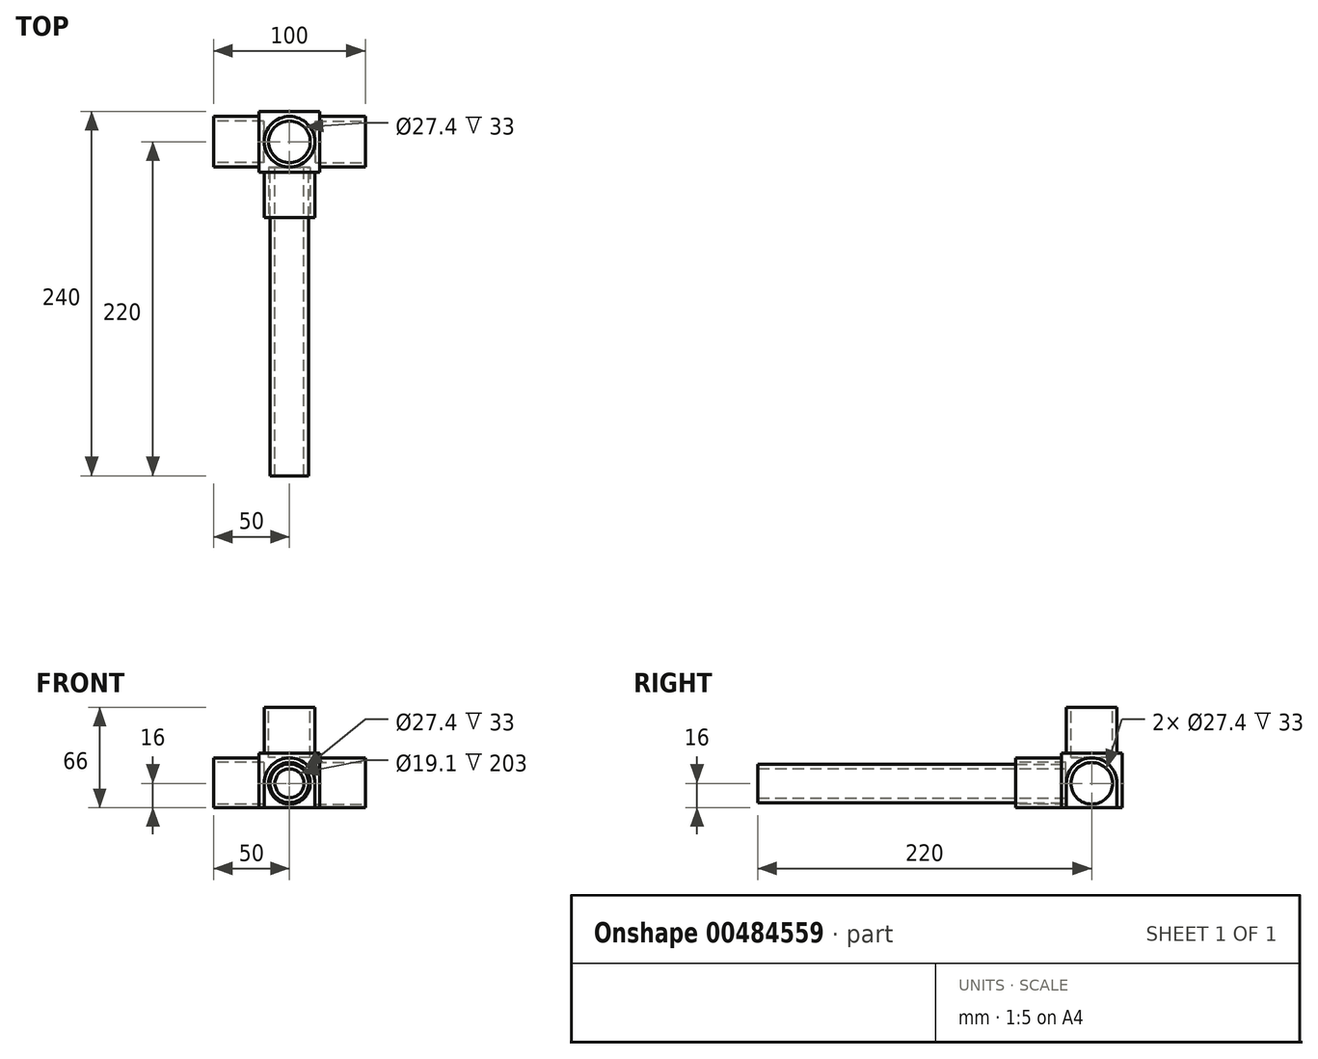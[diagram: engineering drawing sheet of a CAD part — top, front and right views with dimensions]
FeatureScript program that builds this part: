
annotation { "Feature Type Name" : "Feature", "Feature Type Description" : "" }
export const myFeature = defineFeature(function(context is Context, id is Id, definition is map)
    precondition{}
    {
        {
            var Q0;
            Q0=qCreatedBy(makeId("Front.planeOp"),FACE);
            var sketch = newSketch(context, id + "F0", { "sketchPlane" : qUnion([Q0])});
            skLineSegment(sketch, "E0.bottom", {"start": v(20, 20) * mm, "end": v(-20, 20) * mm});
            skLineSegment(sketch, "E0.top", {"start": v(20, -20) * mm, "end": v(-20, -20) * mm});
            skLineSegment(sketch, "E0.left", {"start": v(20, 20) * mm, "end": v(20, -20) * mm});
            skLineSegment(sketch, "E0.right", {"start": v(-20, 20) * mm, "end": v(-20, -20) * mm});
            skPoint(sketch, "E0.middle", {"position": v(0, 0) * mm});
            skSolve(sketch);
        }
        {
            var Q0;
            Q0=makeQuery(id+"F0.imprint","IMPRINT",FACE,{"disambiguationData":[TD([[makeQuery(id+"F0.imprint","IMPRINT",EDGE,{"derivedFrom":sQuery(id+"F0.wireOp",EDGE,"E0.bottom")}),1.0]])]});
            extrude(context, id + "F1", {"entities" : qUnion([Q0]), "endBound" : BoundingType.SYMMETRIC, "depth" : 40 * mm});
        }
        {
            var Q0;
            Q0=makeQuery(id+"F1.opExtrude","CAP_FACE",FACE,{"disambiguationData":[OSD([sQuery(id+"F0.wireOp",EDGE,"E0.bottom"),sQuery(id+"F0.wireOp",EDGE,"E0.top"),sQuery(id+"F0.wireOp",EDGE,"E0.left"),sQuery(id+"F0.wireOp",EDGE,"E0.right")])],"isStart":false});
            var sketch = newSketch(context, id + "F2", { "sketchPlane" : qUnion([Q0])});
            skLineSegment(sketch, "E1.bottom", {"start": v(20, 20) * mm, "end": v(-20, 20) * mm});
            skLineSegment(sketch, "E1.top", {"start": v(20, -20) * mm, "end": v(-20, -20) * mm});
            skLineSegment(sketch, "E1.left", {"start": v(20, 20) * mm, "end": v(20, -20) * mm});
            skLineSegment(sketch, "E1.right", {"start": v(-20, 20) * mm, "end": v(-20, -20) * mm});
            skPoint(sketch, "E1.middle", {"position": v(0, 0) * mm});
            skCircle(sketch, "E2", {"center": v(0, 0) * mm, "radius": 12.7 * mm});
            skCircle(sketch, "E3.0", {"center": v(0, 0) * mm, "radius": 9.55 * mm});
            skCircle(sketch, "E4.0", {"center": v(0, 0) * mm, "radius": 13.7 * mm});
            skCircle(sketch, "E5.0", {"center": v(0, 0) * mm, "radius": 16.7 * mm});
            skSolve(sketch);
        }
        {
            var Q0;
            Q0=makeQuery(id+"F2.imprint","IMPRINT",FACE,{"disambiguationData":[TD([[makeQuery(id+"F2.imprint","IMPRINT",EDGE,{"derivedFrom":sQuery(id+"F2.wireOp",EDGE,"E2")}),-1.0]])]});
            var Q1;
            Q1=makeQuery(id+"F2.imprint","IMPRINT",FACE,{"disambiguationData":[TD([[makeQuery(id+"F2.imprint","IMPRINT",EDGE,{"derivedFrom":sQuery(id+"F2.wireOp",EDGE,"E2")}),1.0]])]});
            var Q2;
            Q2=makeQuery(id+"F2.imprint","IMPRINT",FACE,{"disambiguationData":[TD([[makeQuery(id+"F2.imprint","IMPRINT",EDGE,{"derivedFrom":sQuery(id+"F2.wireOp",EDGE,"E3.0")}),1.0]])]});
            extrude(context, id + "F3", {"entities" : qUnion([Q0, Q1, Q2]), "operationType" : NewBodyOperationType.REMOVE, "oppositeDirection" : true, "depth" : 3 * mm});
        }
        {
            var Q0;
            Q0=makeQuery(id+"F2.imprint","IMPRINT",FACE,{"disambiguationData":[TD([[makeQuery(id+"F2.imprint","IMPRINT",EDGE,{"derivedFrom":sQuery(id+"F2.wireOp",EDGE,"E2")}),1.0]])]});
            extrude(context, id + "F4", {"entities" : qUnion([Q0]), "depth" : 200 * mm});
        }
        {
            var Q0;
            Q0=makeQuery(id+"F4.opExtrude","CAP_FACE",FACE,{"disambiguationData":[OSD([sQuery(id+"F2.wireOp",EDGE,"E2"),sQuery(id+"F2.wireOp",EDGE,"E3.0")])],"isStart":true});
            extrude(context, id + "F5", {"entities" : qUnion([Q0]), "operationType" : NewBodyOperationType.ADD, "depth" : 3 * mm});
        }
        {
            var Q0;
            Q0=makeQuery(id+"F2.imprint","IMPRINT",FACE,{"disambiguationData":[TD([[makeQuery(id+"F2.imprint","IMPRINT",EDGE,{"derivedFrom":sQuery(id+"F2.wireOp",EDGE,"E4.0")}),-1.0]])]});
            extrude(context, id + "F6", {"entities" : qUnion([Q0]), "operationType" : NewBodyOperationType.ADD, "depth" : 30 * mm});
        }
        {
            var Q0;
            Q0=makeQuery(id+"F1.opExtrude","SWEPT_FACE",FACE,{"disambiguationData":[OSD([sQuery(id+"F0.wireOp",EDGE,"E0.left")])]});
            var sketch = newSketch(context, id + "F7", { "sketchPlane" : qUnion([Q0])});
            skLineSegment(sketch, "E6.bottom", {"start": v(20, 20) * mm, "end": v(-20, 20) * mm});
            skLineSegment(sketch, "E6.top", {"start": v(20, -20) * mm, "end": v(-20, -20) * mm});
            skLineSegment(sketch, "E6.left", {"start": v(20, 20) * mm, "end": v(20, -20) * mm});
            skLineSegment(sketch, "E6.right", {"start": v(-20, 20) * mm, "end": v(-20, -20) * mm});
            skPoint(sketch, "E6.middle", {"position": v(0, 0) * mm});
            skCircle(sketch, "E7", {"center": v(0, 0) * mm, "radius": 12.7 * mm});
            skCircle(sketch, "E8.0", {"center": v(0, 0) * mm, "radius": 9.55 * mm});
            skCircle(sketch, "E9.0", {"center": v(0, 0) * mm, "radius": 13.7 * mm});
            skCircle(sketch, "E10.0", {"center": v(0, 0) * mm, "radius": 16.7 * mm});
            skSolve(sketch);
        }
        {
            var Q0;
            Q0=makeQuery(id+"F7.imprint","IMPRINT",FACE,{"disambiguationData":[TD([[makeQuery(id+"F7.imprint","IMPRINT",EDGE,{"derivedFrom":sQuery(id+"F7.wireOp",EDGE,"E7")}),-1.0]])]});
            var Q1;
            Q1=makeQuery(id+"F7.imprint","IMPRINT",FACE,{"disambiguationData":[TD([[makeQuery(id+"F7.imprint","IMPRINT",EDGE,{"derivedFrom":sQuery(id+"F7.wireOp",EDGE,"E7")}),1.0]])]});
            var Q2;
            Q2=makeQuery(id+"F7.imprint","IMPRINT",FACE,{"disambiguationData":[TD([[makeQuery(id+"F7.imprint","IMPRINT",EDGE,{"derivedFrom":sQuery(id+"F7.wireOp",EDGE,"E8.0")}),1.0]])]});
            extrude(context, id + "F8", {"entities" : qUnion([Q0, Q1, Q2]), "operationType" : NewBodyOperationType.REMOVE, "oppositeDirection" : true, "depth" : 3 * mm});
        }
        {
            var Q0;
            Q0=makeQuery(id+"F7.imprint","IMPRINT",FACE,{"disambiguationData":[TD([[makeQuery(id+"F7.imprint","IMPRINT",EDGE,{"derivedFrom":sQuery(id+"F7.wireOp",EDGE,"E7")}),1.0]])]});
            extrude(context, id + "F9", {"entities" : qUnion([Q0]), "depth" : 300 * mm});
        }
        {
            var Q0;
            Q0=makeQuery(id+"F7.imprint","IMPRINT",FACE,{"disambiguationData":[TD([[makeQuery(id+"F7.imprint","IMPRINT",EDGE,{"derivedFrom":sQuery(id+"F7.wireOp",EDGE,"E9.0")}),-1.0]])]});
            extrude(context, id + "F10", {"entities" : qUnion([Q0]), "operationType" : NewBodyOperationType.ADD, "depth" : 30 * mm});
        }
        {
            var Q0;
            Q0=makeQuery(id+"F1.opExtrude","SWEPT_FACE",FACE,{"disambiguationData":[OSD([sQuery(id+"F0.wireOp",EDGE,"E0.right")])]});
            var sketch = newSketch(context, id + "F11", { "sketchPlane" : qUnion([Q0])});
            skLineSegment(sketch, "E11.bottom", {"start": v(20, 20) * mm, "end": v(-20, 20) * mm});
            skLineSegment(sketch, "E11.top", {"start": v(20, -20) * mm, "end": v(-20, -20) * mm});
            skLineSegment(sketch, "E11.left", {"start": v(20, 20) * mm, "end": v(20, -20) * mm});
            skLineSegment(sketch, "E11.right", {"start": v(-20, 20) * mm, "end": v(-20, -20) * mm});
            skPoint(sketch, "E11.middle", {"position": v(0, 0) * mm});
            skCircle(sketch, "E12", {"center": v(0, 0) * mm, "radius": 12.7 * mm});
            skCircle(sketch, "E13.0", {"center": v(0, 0) * mm, "radius": 9.55 * mm});
            skCircle(sketch, "E14.0", {"center": v(0, 0) * mm, "radius": 13.7 * mm});
            skCircle(sketch, "E15.0", {"center": v(0, 0) * mm, "radius": 16.7 * mm});
            skSolve(sketch);
        }
        {
            var Q0;
            Q0=makeQuery(id+"F11.imprint","IMPRINT",FACE,{"disambiguationData":[TD([[makeQuery(id+"F11.imprint","IMPRINT",EDGE,{"derivedFrom":sQuery(id+"F11.wireOp",EDGE,"E12")}),-1.0]])]});
            var Q1;
            Q1=makeQuery(id+"F11.imprint","IMPRINT",FACE,{"disambiguationData":[TD([[makeQuery(id+"F11.imprint","IMPRINT",EDGE,{"derivedFrom":sQuery(id+"F11.wireOp",EDGE,"E12")}),1.0]])]});
            var Q2;
            Q2=makeQuery(id+"F11.imprint","IMPRINT",FACE,{"disambiguationData":[TD([[makeQuery(id+"F11.imprint","IMPRINT",EDGE,{"derivedFrom":sQuery(id+"F11.wireOp",EDGE,"E13.0")}),1.0]])]});
            extrude(context, id + "F12", {"entities" : qUnion([Q0, Q1, Q2]), "operationType" : NewBodyOperationType.REMOVE, "oppositeDirection" : true, "depth" : 3 * mm});
        }
        {
            var Q0;
            Q0=makeQuery(id+"F11.imprint","IMPRINT",FACE,{"disambiguationData":[TD([[makeQuery(id+"F11.imprint","IMPRINT",EDGE,{"derivedFrom":sQuery(id+"F11.wireOp",EDGE,"E12")}),1.0]])]});
            extrude(context, id + "F13", {"entities" : qUnion([Q0]), "depth" : 300 * mm});
        }
        {
            var Q0;
            Q0=makeQuery(id+"F11.imprint","IMPRINT",FACE,{"disambiguationData":[TD([[makeQuery(id+"F11.imprint","IMPRINT",EDGE,{"derivedFrom":sQuery(id+"F11.wireOp",EDGE,"E14.0")}),-1.0]])]});
            extrude(context, id + "F14", {"entities" : qUnion([Q0]), "operationType" : NewBodyOperationType.ADD, "depth" : 30 * mm});
        }
        {
            var Q0;
            Q0=makeQuery(id+"F1.opExtrude","SWEPT_FACE",FACE,{"disambiguationData":[OSD([sQuery(id+"F0.wireOp",EDGE,"E0.bottom")])]});
            var sketch = newSketch(context, id + "F15", { "sketchPlane" : qUnion([Q0])});
            skLineSegment(sketch, "E16.bottom", {"start": v(20, 20) * mm, "end": v(-20, 20) * mm});
            skLineSegment(sketch, "E16.top", {"start": v(20, -20) * mm, "end": v(-20, -20) * mm});
            skLineSegment(sketch, "E16.left", {"start": v(20, 20) * mm, "end": v(20, -20) * mm});
            skLineSegment(sketch, "E16.right", {"start": v(-20, 20) * mm, "end": v(-20, -20) * mm});
            skPoint(sketch, "E16.middle", {"position": v(0, 0) * mm});
            skCircle(sketch, "E17", {"center": v(0, 0) * mm, "radius": 12.7 * mm});
            skCircle(sketch, "E18.0", {"center": v(0, 0) * mm, "radius": 9.55 * mm});
            skCircle(sketch, "E19.0", {"center": v(0, 0) * mm, "radius": 13.7 * mm});
            skCircle(sketch, "E20.0", {"center": v(0, 0) * mm, "radius": 16.7 * mm});
            skSolve(sketch);
        }
        {
            var Q0;
            Q0=makeQuery(id+"F15.imprint","IMPRINT",FACE,{"disambiguationData":[TD([[makeQuery(id+"F15.imprint","IMPRINT",EDGE,{"derivedFrom":sQuery(id+"F15.wireOp",EDGE,"E17")}),-1.0]])]});
            var Q1;
            Q1=makeQuery(id+"F15.imprint","IMPRINT",FACE,{"disambiguationData":[TD([[makeQuery(id+"F15.imprint","IMPRINT",EDGE,{"derivedFrom":sQuery(id+"F15.wireOp",EDGE,"E17")}),1.0]])]});
            var Q2;
            Q2=makeQuery(id+"F15.imprint","IMPRINT",FACE,{"disambiguationData":[TD([[makeQuery(id+"F15.imprint","IMPRINT",EDGE,{"derivedFrom":sQuery(id+"F15.wireOp",EDGE,"E18.0")}),1.0]])]});
            extrude(context, id + "F16", {"entities" : qUnion([Q0, Q1, Q2]), "operationType" : NewBodyOperationType.REMOVE, "oppositeDirection" : true, "depth" : 3 * mm});
        }
        {
            var Q0;
            Q0=makeQuery(id+"F15.imprint","IMPRINT",FACE,{"disambiguationData":[TD([[makeQuery(id+"F15.imprint","IMPRINT",EDGE,{"derivedFrom":sQuery(id+"F15.wireOp",EDGE,"E17")}),1.0]])]});
            extrude(context, id + "F17", {"entities" : qUnion([Q0]), "depth" : 300 * mm});
        }
        {
            var Q0;
            Q0=makeQuery(id+"F15.imprint","IMPRINT",FACE,{"disambiguationData":[TD([[makeQuery(id+"F15.imprint","IMPRINT",EDGE,{"derivedFrom":sQuery(id+"F15.wireOp",EDGE,"E19.0")}),-1.0]])]});
            extrude(context, id + "F18", {"entities" : qUnion([Q0]), "operationType" : NewBodyOperationType.ADD, "depth" : 30 * mm});
        }
        {
            var Q0;
            Q0=makeQuery(id+"F1.opExtrude","SWEPT_FACE",FACE,{"disambiguationData":[OSD([sQuery(id+"F0.wireOp",EDGE,"E0.right")])]});
            var sketch = newSketch(context, id + "F19", { "sketchPlane" : qUnion([Q0])});
            skLineSegment(sketch, "E21", {"start": v(-16.7, 0) * mm, "end": v(-16.7, -20) * mm});
            skLineSegment(sketch, "E22", {"start": v(16.7, 0) * mm, "end": v(16.7, -20) * mm});
            skLineSegment(sketch, "E23", {"start": v(16.7, -20) * mm, "end": v(-16.7, -20) * mm});
            skSolve(sketch);
        }
        {
            var Q0;
            Q0=makeQuery(id+"F1.opExtrude","CAP_FACE",FACE,{"disambiguationData":[OSD([sQuery(id+"F0.wireOp",EDGE,"E0.bottom"),sQuery(id+"F0.wireOp",EDGE,"E0.top"),sQuery(id+"F0.wireOp",EDGE,"E0.left"),sQuery(id+"F0.wireOp",EDGE,"E0.right")])],"isStart":false});
            var sketch = newSketch(context, id + "F20", { "sketchPlane" : qUnion([Q0])});
            skLineSegment(sketch, "E24", {"start": v(-16.7, 0) * mm, "end": v(-16.7, -20) * mm});
            skPoint(sketch, "E24.startSnap0", {"position": v(-20, 0) * mm});
            skLineSegment(sketch, "E25", {"start": v(16.7, 0) * mm, "end": v(16.7, -20) * mm});
            skLineSegment(sketch, "E26", {"start": v(16.7, -20) * mm, "end": v(-16.7, -20) * mm});
            skSolve(sketch);
        }
        {
            var Q0;
            {var subQ0=sQuery(id+"F19.wireOp",EDGE,"E21");Q0=makeQuery(id+"F19.imprint","IMPRINT",FACE,{"disambiguationData":[TD([[makeQuery(id+"F19.imprint","IMPRINT",EDGE,{"derivedFrom":subQ0}),1.0]])]});}
            var Q1;
            Q1=makeQuery(id+"F14.opExtrude","CAP_FACE",FACE,{"disambiguationData":[OSD([sQuery(id+"F11.wireOp",EDGE,"E14.0"),sQuery(id+"F11.wireOp",EDGE,"E15.0")])],"isStart":false});
            extrude(context, id + "F21", {"entities" : qUnion([Q0]), "operationType" : NewBodyOperationType.ADD, "endBound" : BoundingType.UP_TO_SURFACE, "endBoundEntityFace" : qUnion([Q1]), "depth" : 25 * mm});
        }
        {
            var Q0;
            {var subQ0=sQuery(id+"F20.wireOp",EDGE,"E24");Q0=makeQuery(id+"F20.imprint","IMPRINT",FACE,{"disambiguationData":[TD([[makeQuery(id+"F20.imprint","IMPRINT",EDGE,{"derivedFrom":subQ0}),1.0]])]});}
            var Q1;
            Q1=makeQuery(id+"F6.opExtrude","CAP_FACE",FACE,{"disambiguationData":[OSD([sQuery(id+"F2.wireOp",EDGE,"E4.0"),sQuery(id+"F2.wireOp",EDGE,"E5.0")])],"isStart":false});
            extrude(context, id + "F22", {"entities" : qUnion([Q0]), "operationType" : NewBodyOperationType.ADD, "endBound" : BoundingType.UP_TO_SURFACE, "endBoundEntityFace" : qUnion([Q1]), "depth" : 25 * mm});
        }
        {
            var Q0;
            Q0=makeQuery(id+"F1.opExtrude","SWEPT_FACE",FACE,{"disambiguationData":[OSD([sQuery(id+"F0.wireOp",EDGE,"E0.left")])]});
            var sketch = newSketch(context, id + "F23", { "sketchPlane" : qUnion([Q0])});
            skLineSegment(sketch, "E27", {"start": v(-16.7, 0) * mm, "end": v(-16.7, -20) * mm});
            skLineSegment(sketch, "E28", {"start": v(16.7, 0) * mm, "end": v(16.7, -20) * mm});
            skLineSegment(sketch, "E29", {"start": v(16.7, -20) * mm, "end": v(-16.7, -20) * mm});
            skSolve(sketch);
        }
        {
            var Q0;
            {var subQ0=sQuery(id+"F23.wireOp",EDGE,"E27");Q0=makeQuery(id+"F23.imprint","IMPRINT",FACE,{"disambiguationData":[TD([[makeQuery(id+"F23.imprint","IMPRINT",EDGE,{"derivedFrom":subQ0}),1.0]])]});}
            var Q1;
            Q1=makeQuery(id+"F10.opExtrude","CAP_FACE",FACE,{"disambiguationData":[OSD([sQuery(id+"F7.wireOp",EDGE,"E9.0"),sQuery(id+"F7.wireOp",EDGE,"E10.0")])],"isStart":false});
            extrude(context, id + "F24", {"entities" : qUnion([Q0]), "operationType" : NewBodyOperationType.ADD, "endBound" : BoundingType.UP_TO_SURFACE, "endBoundEntityFace" : qUnion([Q1]), "depth" : 25 * mm});
        }
        {
            var Q0;
            Q0=makeQuery(id+"F24.boolean.opBoolean","MERGE",FACE,{"derivedFrom":[makeQuery(id+"F22.boolean.opBoolean","MERGE",FACE,{"derivedFrom":[makeQuery(id+"F21.boolean.opBoolean","MERGE",FACE,{"derivedFrom":[makeQuery(id+"F1.opExtrude","SWEPT_FACE",FACE,{"disambiguationData":[OSD([sQuery(id+"F0.wireOp",EDGE,"E0.top")])]}),makeQuery(id+"F21.opExtrude","SWEPT_FACE",FACE,{"disambiguationData":[OSD([sQuery(id+"F19.wireOp",EDGE,"E23")])]})]}),makeQuery(id+"F22.opExtrude","SWEPT_FACE",FACE,{"disambiguationData":[OSD([sQuery(id+"F20.wireOp",EDGE,"E26")])]})]}),makeQuery(id+"F24.opExtrude","SWEPT_FACE",FACE,{"disambiguationData":[OSD([sQuery(id+"F23.wireOp",EDGE,"E29")])]})]});
            extrude(context, id + "F25", {"entities" : qUnion([Q0]), "operationType" : NewBodyOperationType.REMOVE, "oppositeDirection" : true, "depth" : 4 * mm});
        }
        {
            var Q0;
            Q0=makeQuery(id+"F1.opExtrude","SWEPT_BODY",BODY,{"disambiguationData":[OSD([sQuery(id+"F0.wireOp",EDGE,"E0.bottom"),sQuery(id+"F0.wireOp",EDGE,"E0.top"),sQuery(id+"F0.wireOp",EDGE,"E0.left"),sQuery(id+"F0.wireOp",EDGE,"E0.right")])]});
            transform(context, id + "F26", {"entities" : qUnion([Q0]), "transformType" : TransformType.TRANSLATION_3D, "dx" : 0 * mm, "dy" : 0 * mm, "dz" : 0 * mm, "makeCopy" : true});
        }
        {
            var Q0;
            Q0=makeQuery(id+"F4.opExtrude","SWEPT_BODY",BODY,{"disambiguationData":[OSD([sQuery(id+"F2.wireOp",EDGE,"E2"),sQuery(id+"F2.wireOp",EDGE,"E3.0")])]});
            var Q1;
            Q1=makeQuery(id+"F9.opExtrude","SWEPT_BODY",BODY,{"disambiguationData":[OSD([sQuery(id+"F7.wireOp",EDGE,"E7"),sQuery(id+"F7.wireOp",EDGE,"E8.0")])]});
            var Q2;
            Q2=makeQuery(id+"F13.opExtrude","SWEPT_BODY",BODY,{"disambiguationData":[OSD([sQuery(id+"F11.wireOp",EDGE,"E12"),sQuery(id+"F11.wireOp",EDGE,"E13.0")])]});
            var Q3;
            Q3=makeQuery(id+"F17.opExtrude","SWEPT_BODY",BODY,{"disambiguationData":[OSD([sQuery(id+"F15.wireOp",EDGE,"E17"),sQuery(id+"F15.wireOp",EDGE,"E18.0")])]});
            var Q4;
            Q4=makeQuery(id+"F26.opPattern","COPY",BODY,{"derivedFrom":makeQuery(id+"F1.opExtrude","SWEPT_BODY",BODY,{"disambiguationData":[OSD([sQuery(id+"F0.wireOp",EDGE,"E0.bottom"),sQuery(id+"F0.wireOp",EDGE,"E0.top"),sQuery(id+"F0.wireOp",EDGE,"E0.left"),sQuery(id+"F0.wireOp",EDGE,"E0.right")])]}),"instanceName":"1"});
            deleteBodies(context, id + "F27", {"entities" : qUnion([Q0, Q1, Q2, Q3, Q4])});
        }
    });
